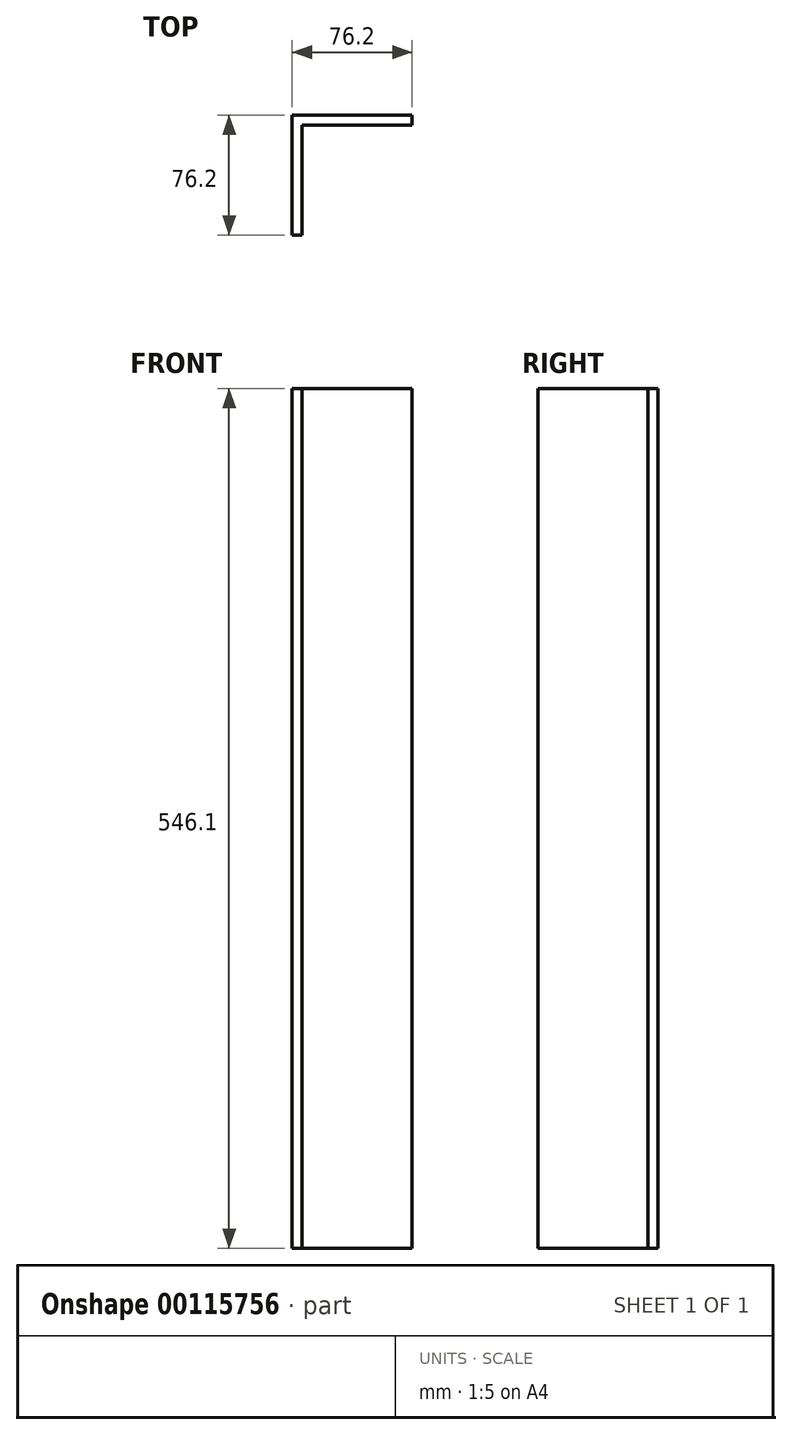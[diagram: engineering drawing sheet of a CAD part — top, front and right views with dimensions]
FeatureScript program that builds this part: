
annotation { "Feature Type Name" : "Feature", "Feature Type Description" : "" }
export const myFeature = defineFeature(function(context is Context, id is Id, definition is map)
    precondition{}
    {
        {
            var Q0;
            Q0=qCreatedBy(makeId("Top.planeOp"),FACE);
            var sketch = newSketch(context, id + "F0", { "sketchPlane" : qUnion([Q0])});
            skLineSegment(sketch, "E0", {"start": v(0, -76.2) * mm, "end": v(0, 0) * mm});
            skLineSegment(sketch, "E1", {"start": v(0, 0) * mm, "end": v(76.2, 0) * mm});
            skLineSegment(sketch, "E2.0", {"start": v(6.35, -6.35) * mm, "end": v(76.2, -6.35) * mm});
            skLineSegment(sketch, "E2.1", {"start": v(6.35, -76.2) * mm, "end": v(6.35, -6.35) * mm});
            skLineSegment(sketch, "E3", {"start": v(0, -76.2) * mm, "end": v(6.35, -76.2) * mm});
            skLineSegment(sketch, "E4", {"start": v(76.2, -6.35) * mm, "end": v(76.2, 0) * mm});
            skSolve(sketch);
        }
        {
            var Q0;
            Q0 = qSketchRegion(id + "F0", true);
            extrude(context, id + "F1", {"entities" : qUnion([Q0]), "oppositeDirection" : true, "depth" : 546.1 * mm});
        }
    });
